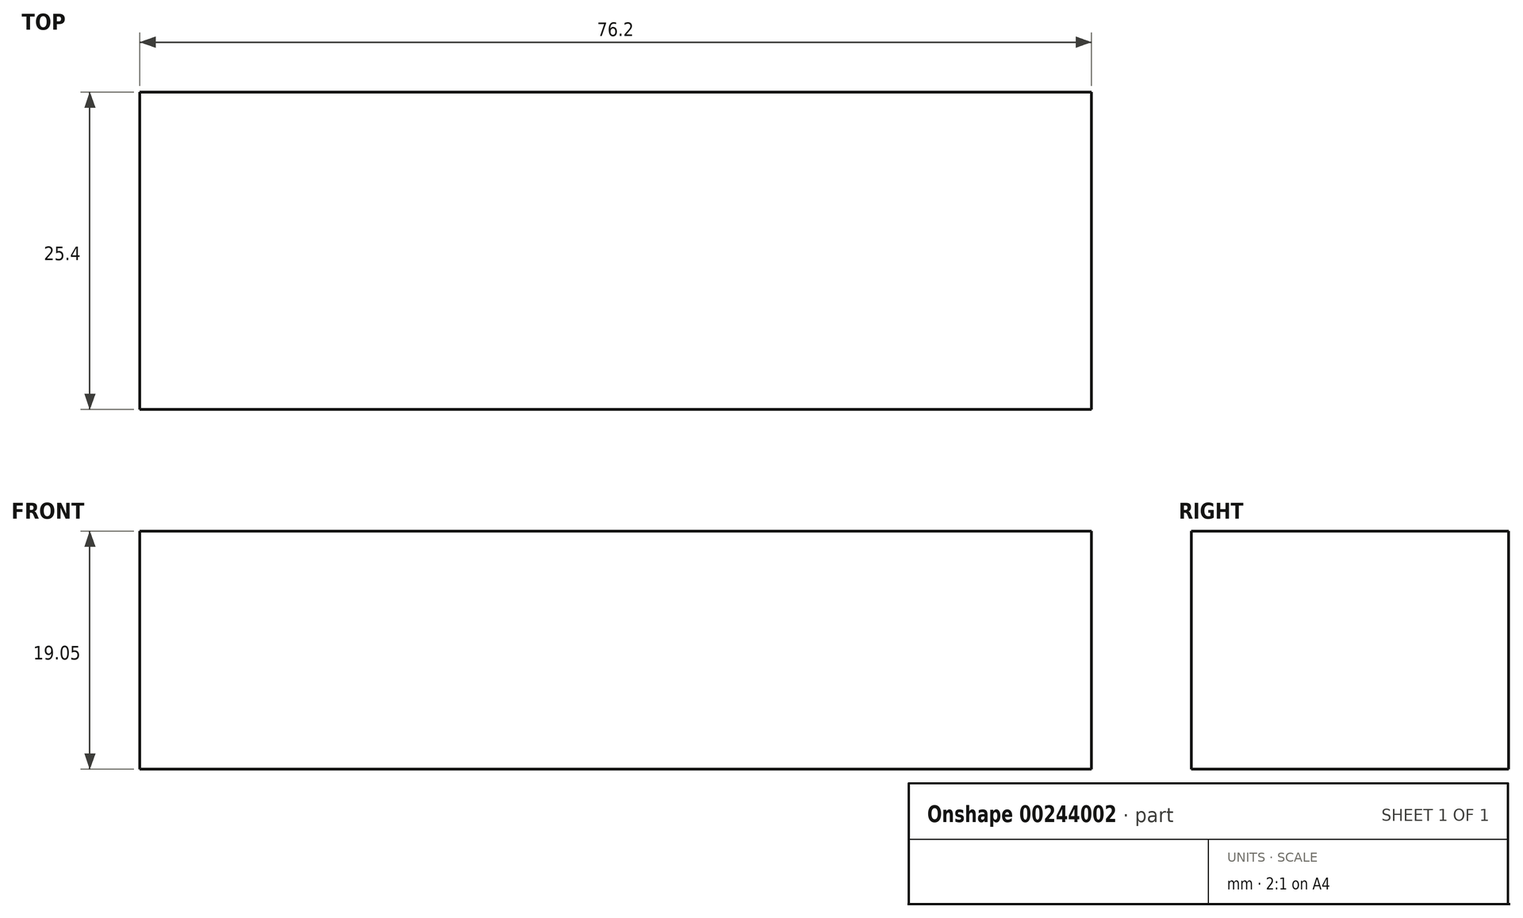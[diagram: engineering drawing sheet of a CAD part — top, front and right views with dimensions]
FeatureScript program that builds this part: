
annotation { "Feature Type Name" : "Feature", "Feature Type Description" : "" }
export const myFeature = defineFeature(function(context is Context, id is Id, definition is map)
    precondition{}
    {
        {
            var Q0;
            Q0=qCreatedBy(makeId("Front.planeOp"),FACE);
            var sketch = newSketch(context, id + "F0", { "sketchPlane" : qUnion([Q0])});
            skLineSegment(sketch, "E0.bottom", {"start": v(0, 0) * mm, "end": v(-76.2, 0) * mm});
            skLineSegment(sketch, "E0.top", {"start": v(0, -19.05) * mm, "end": v(-76.2, -19.05) * mm});
            skLineSegment(sketch, "E0.left", {"start": v(0, 0) * mm, "end": v(0, -19.05) * mm});
            skLineSegment(sketch, "E0.right", {"start": v(-76.2, 0) * mm, "end": v(-76.2, -19.05) * mm});
            skLineSegment(sketch, "E1.bottom", {"start": v(0, 0) * mm, "end": v(-23.83, 0) * mm});
            skLineSegment(sketch, "E1.top", {"start": v(0, 50.8) * mm, "end": v(-23.83, 50.8) * mm});
            skLineSegment(sketch, "E1.left", {"start": v(0, 0) * mm, "end": v(0, 50.8) * mm});
            skLineSegment(sketch, "E1.right", {"start": v(-23.83, 22.23) * mm, "end": v(-23.83, 50.8) * mm});
            skLineSegment(sketch, "E2.bottom", {"start": v(-76.2, 0) * mm, "end": v(-52.37, 0) * mm});
            skLineSegment(sketch, "E2.top", {"start": v(-76.2, 50.8) * mm, "end": v(-52.37, 50.8) * mm});
            skLineSegment(sketch, "E2.left", {"start": v(-76.2, 0) * mm, "end": v(-76.2, 50.8) * mm});
            skLineSegment(sketch, "E2.right", {"start": v(-52.37, 22.23) * mm, "end": v(-52.37, 50.8) * mm});
            skLineSegment(sketch, "E3.bottom", {"start": v(-52.37, 0) * mm, "end": v(-23.83, 0) * mm});
            skLineSegment(sketch, "E3.top", {"start": v(-52.37, 22.23) * mm, "end": v(-23.83, 22.23) * mm});
            skSolve(sketch);
        }
        {
            var Q0;
            Q0=makeQuery(id+"F0.imprint","IMPRINT",FACE,{"disambiguationData":[TD([[makeQuery(id+"F0.imprint","IMPRINT",EDGE,{"derivedFrom":sQuery(id+"F0.wireOp",EDGE,"E1.bottom")}),-1.0]])]});
            var Q1;
            Q1=makeQuery(id+"F0.imprint","IMPRINT",FACE,{"disambiguationData":[TD([[makeQuery(id+"F0.imprint","IMPRINT",EDGE,{"derivedFrom":sQuery(id+"F0.wireOp",EDGE,"E0.top")}),-1.0]])]});
            extrude(context, id + "F1", {"entities" : qUnion([Q0, Q1]), "depth" : 25.4 * mm});
        }
    });
